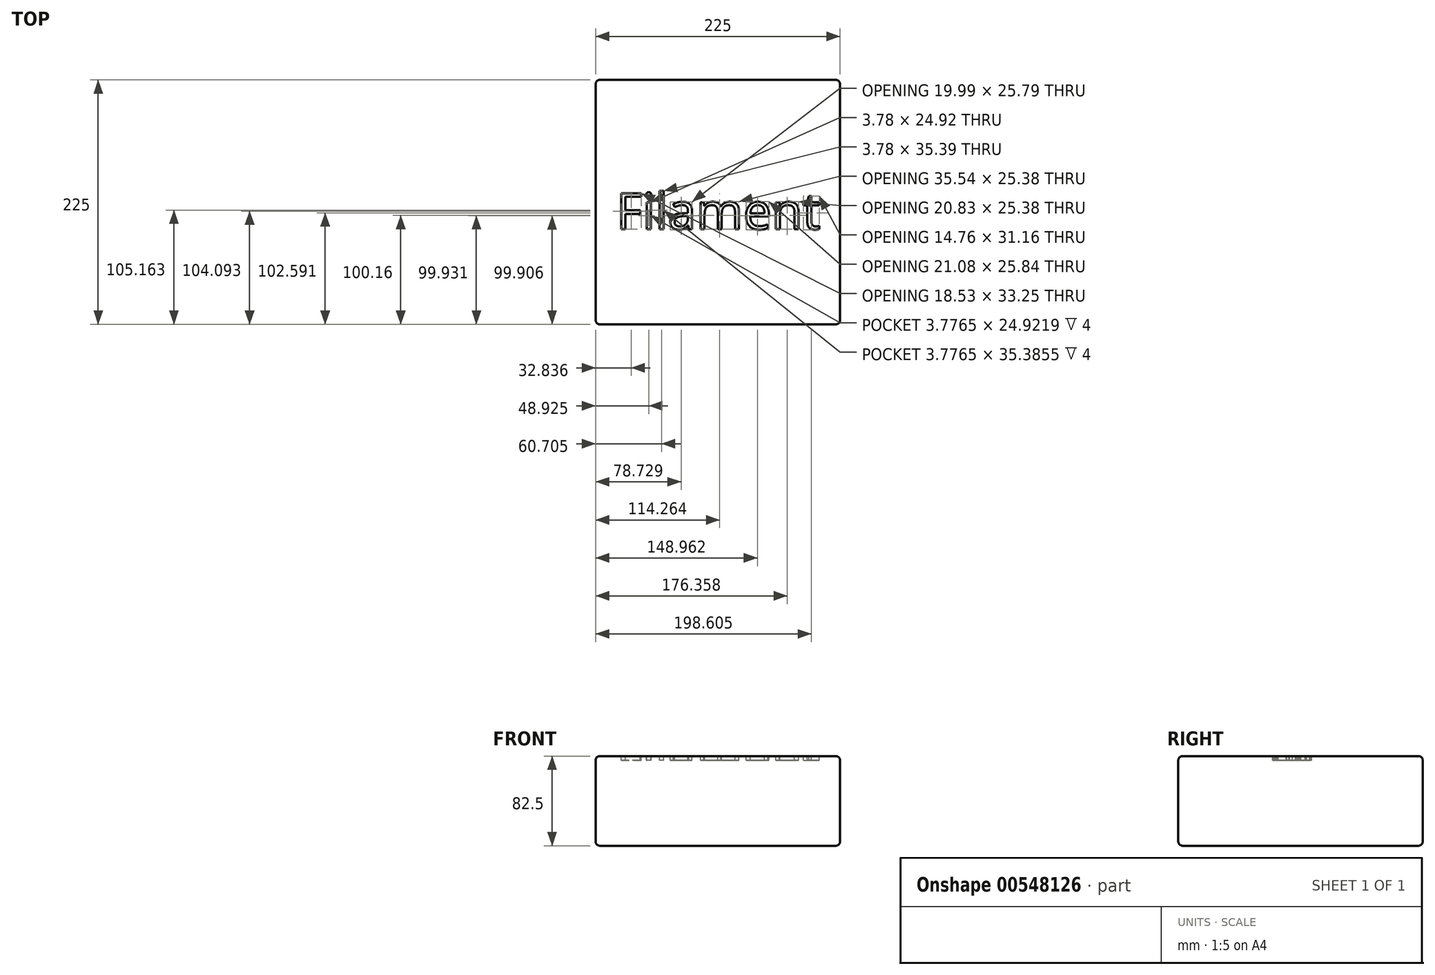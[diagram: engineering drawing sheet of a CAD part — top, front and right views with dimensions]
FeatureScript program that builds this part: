
annotation { "Feature Type Name" : "Feature", "Feature Type Description" : "" }
export const myFeature = defineFeature(function(context is Context, id is Id, definition is map)
    precondition{}
    {
        {
            var Q0;
            Q0=qCreatedBy(makeId("Top.planeOp"),FACE);
            var sketch = newSketch(context, id + "F0", { "sketchPlane" : qUnion([Q0])});
            skLineSegment(sketch, "E0.bottom", {"start": v(0, 0) * mm, "end": v(-225, 0) * mm});
            skLineSegment(sketch, "E0.top", {"start": v(0, 225) * mm, "end": v(-225, 225) * mm});
            skLineSegment(sketch, "E0.left", {"start": v(0, 0) * mm, "end": v(0, 225) * mm});
            skLineSegment(sketch, "E0.right", {"start": v(-225, 0) * mm, "end": v(-225, 225) * mm});
            skSolve(sketch);
        }
        {
            var Q0;
            Q0=makeQuery(id+"F0.imprint","IMPRINT",FACE,{"disambiguationData":[TD([[makeQuery(id+"F0.imprint","IMPRINT",EDGE,{"derivedFrom":sQuery(id+"F0.wireOp",EDGE,"E0.bottom")}),-1.0]])]});
            extrude(context, id + "F1", {"entities" : qUnion([Q0]), "depth" : 82.5 * mm, "offsetDistance" : 25 * mm});
        }
        {
            var Q0;
            Q0=makeQuery(id+"F1.opExtrude","SWEPT_FACE",FACE,{"disambiguationData":[OSD([sQuery(id+"F0.wireOp",EDGE,"E0.bottom")])]});
            var Q1;
            Q1=makeQuery(id+"F1.opExtrude","SWEPT_FACE",FACE,{"disambiguationData":[OSD([sQuery(id+"F0.wireOp",EDGE,"E0.left")])]});
            var Q2;
            Q2=makeQuery(id+"F1.opExtrude","CAP_FACE",FACE,{"disambiguationData":[OSD([sQuery(id+"F0.wireOp",EDGE,"E0.bottom"),sQuery(id+"F0.wireOp",EDGE,"E0.top"),sQuery(id+"F0.wireOp",EDGE,"E0.left"),sQuery(id+"F0.wireOp",EDGE,"E0.right")])],"isStart":false});
            var Q3;
            Q3=makeQuery(id+"F1.opExtrude","SWEPT_FACE",FACE,{"disambiguationData":[OSD([sQuery(id+"F0.wireOp",EDGE,"E0.right")])]});
            var Q4;
            Q4=makeQuery(id+"F1.opExtrude","SWEPT_FACE",FACE,{"disambiguationData":[OSD([sQuery(id+"F0.wireOp",EDGE,"E0.top")])]});
            var Q5;
            Q5=makeQuery(id+"F1.opExtrude","CAP_FACE",FACE,{"disambiguationData":[OSD([sQuery(id+"F0.wireOp",EDGE,"E0.bottom"),sQuery(id+"F0.wireOp",EDGE,"E0.top"),sQuery(id+"F0.wireOp",EDGE,"E0.left"),sQuery(id+"F0.wireOp",EDGE,"E0.right")])],"isStart":true});
            fillet(context, id + "F2", {"entities" : qUnion([Q0, Q1, Q2, Q3, Q4, Q5]), "radius" : 4 * mm, "tangentPropagation" : true, "allowEdgeOverflow" : false});
        }
        {
            var Q0;
            Q0=makeQuery(id+"F1.opExtrude","CAP_FACE",FACE,{"disambiguationData":[OSD([sQuery(id+"F0.wireOp",EDGE,"E0.bottom"),sQuery(id+"F0.wireOp",EDGE,"E0.top"),sQuery(id+"F0.wireOp",EDGE,"E0.left"),sQuery(id+"F0.wireOp",EDGE,"E0.right")])],"isStart":false});
            var sketch = newSketch(context, id + "F3", { "sketchPlane" : qUnion([Q0])});
            skText(sketch, "E1", { "text": "Filament", "fontName": "OpenSans-Regular.ttf"});
            const initialGuessF3  = {"E1": [-0.206, 0.08747, 1, 0, 0.03353]};
            skSetInitialGuess(sketch, initialGuessF3);
            skSolve(sketch);
        }
        {
            var Q0;
            Q0=qSketchRegion(id+"F3",true);
            extrude(context, id + "F4", {"entities" : qUnion([Q0]), "operationType" : NewBodyOperationType.REMOVE, "oppositeDirection" : true, "depth" : 4 * mm, "offsetDistance" : 25 * mm});
        }
    });
